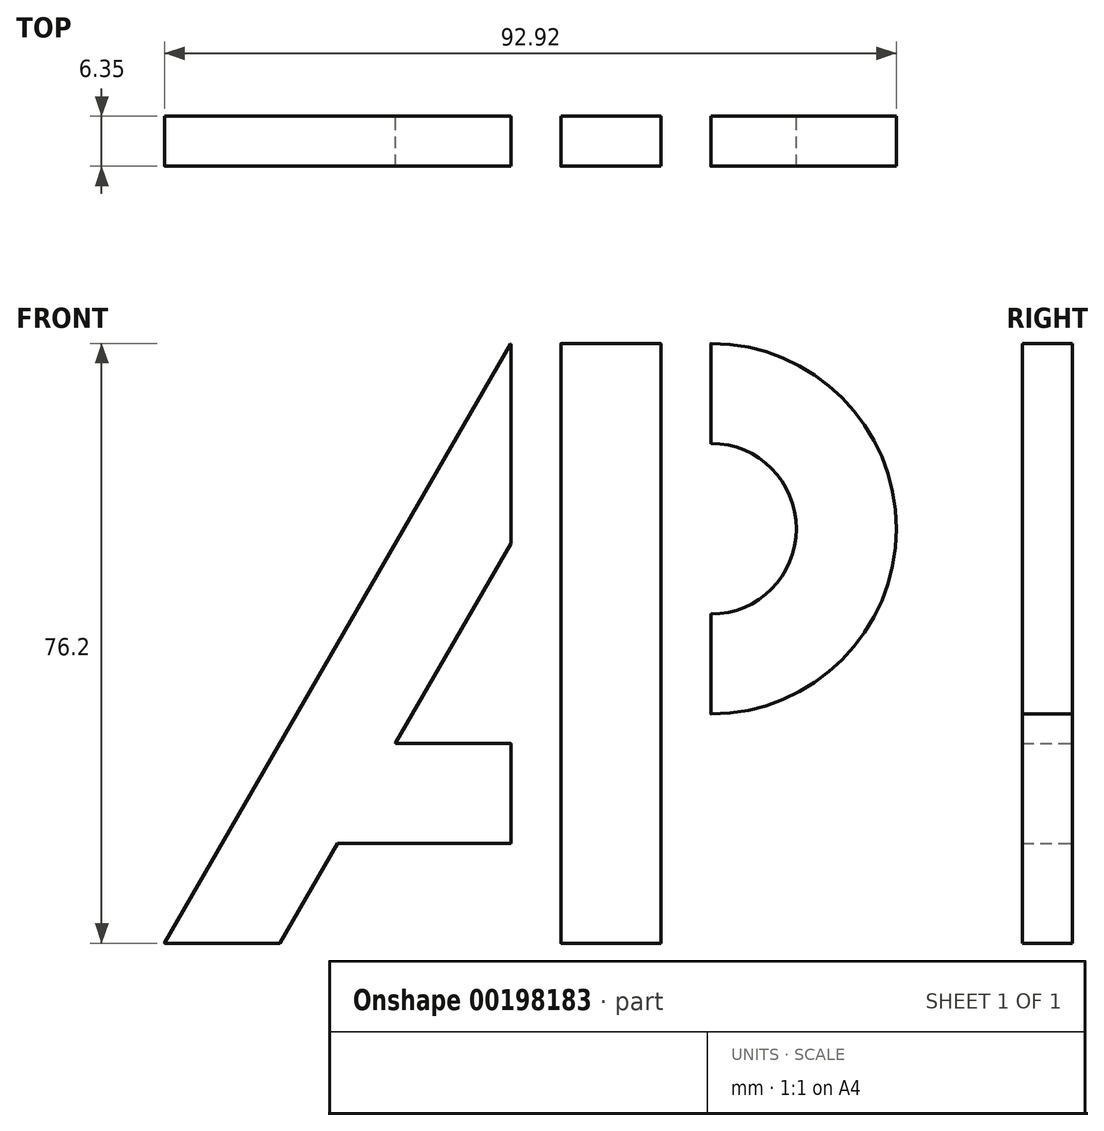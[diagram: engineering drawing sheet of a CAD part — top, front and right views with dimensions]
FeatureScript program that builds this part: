
annotation { "Feature Type Name" : "Feature", "Feature Type Description" : "" }
export const myFeature = defineFeature(function(context is Context, id is Id, definition is map)
    precondition{}
    {
        {
            assignVariable(context, id + "F0", {"name" : "CORNERS", "anyValue" : 1 / 32});
        }
        {
            var Q0;
            Q0=qCreatedBy(makeId("Front.planeOp"),FACE);
            var sketch = newSketch(context, id + "F1", { "sketchPlane" : qUnion([Q0])});
            skLineSegment(sketch, "E0.bottom", {"start": v(-6.35, 38.1) * mm, "end": v(6.35, 38.1) * mm});
            skLineSegment(sketch, "E0.top", {"start": v(-6.35, -38.1) * mm, "end": v(6.35, -38.1) * mm});
            skLineSegment(sketch, "E0.left", {"start": v(-6.35, 38.1) * mm, "end": v(-6.35, -38.1) * mm});
            skLineSegment(sketch, "E0.right", {"start": v(6.35, 38.1) * mm, "end": v(6.35, -38.1) * mm});
            skPoint(sketch, "E0.middle", {"position": v(0, 0) * mm});
            skLineSegment(sketch, "E1.bottom", {"start": v(6.35, 38.1) * mm, "end": v(12.7, 38.1) * mm});
            skLineSegment(sketch, "E1.top", {"start": v(6.35, 25.4) * mm, "end": v(12.7, 25.4) * mm});
            skLineSegment(sketch, "E1.left", {"start": v(6.35, 38.1) * mm, "end": v(6.35, 25.4) * mm});
            skLineSegment(sketch, "E1.right", {"start": v(12.7, 38.1) * mm, "end": v(12.7, 25.4) * mm});
            skLineSegment(sketch, "E2.bottom", {"start": v(6.35, 3.7) * mm, "end": v(12.7, 3.7) * mm});
            skLineSegment(sketch, "E2.top", {"start": v(6.35, -9) * mm, "end": v(12.7, -9) * mm});
            skLineSegment(sketch, "E2.left", {"start": v(6.35, 3.7) * mm, "end": v(6.35, -9) * mm});
            skLineSegment(sketch, "E2.right", {"start": v(12.7, 3.7) * mm, "end": v(12.7, -9) * mm});
            skLineSegment(sketch, "E3.bottom", {"start": v(-6.35, 38.1) * mm, "end": v(-12.7, 38.1) * mm});
            skLineSegment(sketch, "E3.top", {"start": v(-6.35, 12.7) * mm, "end": v(-12.7, 12.7) * mm});
            skLineSegment(sketch, "E3.left", {"start": v(-6.35, 38.1) * mm, "end": v(-6.35, 12.7) * mm});
            skLineSegment(sketch, "E3.right", {"start": v(-12.7, 38.1) * mm, "end": v(-12.7, 12.7) * mm});
            skLineSegment(sketch, "E4.bottom", {"start": v(-6.35, -38.1) * mm, "end": v(-12.7, -38.1) * mm});
            skLineSegment(sketch, "E4.top", {"start": v(-6.35, -25.4) * mm, "end": v(-12.7, -25.4) * mm});
            skLineSegment(sketch, "E4.left", {"start": v(-6.35, -38.1) * mm, "end": v(-6.35, -25.4) * mm});
            skLineSegment(sketch, "E4.right", {"start": v(-12.7, -38.1) * mm, "end": v(-12.7, -25.4) * mm});
            skArc(sketch, "E5", {"start": v(12.7, 3.7) * mm, "mid": v(23.55, 14.55) * mm, "end": v(12.7, 25.4) * mm});
            skArc(sketch, "E6", {"start": v(12.7, -9) * mm, "mid": v(36.25, 14.55) * mm, "end": v(12.7, 38.1) * mm});
            skLineSegment(sketch, "E7", {"start": v(-12.7, -38.1) * mm, "end": v(-56.7, -38.1) * mm});
            skLineSegment(sketch, "E8", {"start": v(-56.7, -38.1) * mm, "end": v(-12.7, 38.1) * mm});
            skLineSegment(sketch, "E9", {"start": v(-12.7, 12.7) * mm, "end": v(-34.7, -25.4) * mm});
            skLineSegment(sketch, "E10", {"start": v(-34.7, -25.4) * mm, "end": v(-12.7, -25.4) * mm});
            skLineSegment(sketch, "E11", {"start": v(-12.7, -25.4) * mm, "end": v(-12.7, -12.7) * mm});
            skLineSegment(sketch, "E12", {"start": v(-12.7, -12.7) * mm, "end": v(-6.35, -12.7) * mm});
            skLineSegment(sketch, "E13", {"start": v(-12.7, -12.7) * mm, "end": v(-27.36, -12.7) * mm});
            skLineSegment(sketch, "E14", {"start": v(-34.7, -25.4) * mm, "end": v(-42.03, -38.1) * mm});
            skSolve(sketch);
        }
        {
            var Q0;
            Q0=makeQuery(id+"F1.imprint","IMPRINT",FACE,{"disambiguationData":[TD([[makeQuery(id+"F1.imprint","IMPRINT",EDGE,{"derivedFrom":sQuery(id+"F1.wireOp",EDGE,"E3.right")}),-1.0]])]});
            var Q1;
            Q1=makeQuery(id+"F1.imprint","IMPRINT",FACE,{"disambiguationData":[TD([[makeQuery(id+"F1.imprint","IMPRINT",EDGE,{"derivedFrom":sQuery(id+"F1.wireOp",EDGE,"E0.bottom")}),-1.0]])]});
            var Q2;
            Q2=makeQuery(id+"F1.imprint","IMPRINT",FACE,{"disambiguationData":[TD([[makeQuery(id+"F1.imprint","IMPRINT",EDGE,{"derivedFrom":sQuery(id+"F1.wireOp",EDGE,"E1.right")}),1.0]])]});
            var Q3;
            {var subQ0=sQuery(id+"F1.wireOp",EDGE,"E10");Q3=makeQuery(id+"F1.imprint","IMPRINT",FACE,{"disambiguationData":[TD([[makeQuery(id+"F1.imprint","IMPRINT",EDGE,{"derivedFrom":subQ0}),1.0]])]});}
            extrude(context, id + "F2", {"entities" : qUnion([Q0, Q1, Q2, Q3]), "depth" : 6.35 * mm});
        }
        {
            var Q0;
            Q0=makeQuery(id+"F2.opExtrude","SWEPT_EDGE",EDGE,{"disambiguationData":[OSD([sQuery(id+"F1.wireOp",EDGE,"E3.bottom"),sQuery(id+"F1.wireOp",EDGE,"E3.right"),sQuery(id+"F1.wireOp",EDGE,"E8")])]});
            var Q1;
            Q1=makeQuery(id+"F2.opExtrude","SWEPT_EDGE",EDGE,{"disambiguationData":[OSD([sQuery(id+"F1.wireOp",EDGE,"E3.top"),sQuery(id+"F1.wireOp",EDGE,"E3.right"),sQuery(id+"F1.wireOp",EDGE,"E9")])]});
            var Q2;
            Q2=makeQuery(id+"F2.opExtrude","SWEPT_EDGE",EDGE,{"disambiguationData":[OSD([sQuery(id+"F1.wireOp",EDGE,"E4.top"),sQuery(id+"F1.wireOp",EDGE,"E4.right"),sQuery(id+"F1.wireOp",EDGE,"E10"),sQuery(id+"F1.wireOp",EDGE,"E11")])]});
            var Q3;
            Q3=makeQuery(id+"F2.opExtrude","SWEPT_EDGE",EDGE,{"disambiguationData":[OSD([sQuery(id+"F1.wireOp",EDGE,"E9"),sQuery(id+"F1.wireOp",EDGE,"E10"),sQuery(id+"F1.wireOp",EDGE,"E14")])]});
            var Q4;
            Q4=makeQuery(id+"F2.opExtrude","SWEPT_EDGE",EDGE,{"disambiguationData":[OSD([sQuery(id+"F1.wireOp",EDGE,"E7"),sQuery(id+"F1.wireOp",EDGE,"E14")])]});
            var Q5;
            Q5=makeQuery(id+"F2.opExtrude","SWEPT_EDGE",EDGE,{"disambiguationData":[OSD([sQuery(id+"F1.wireOp",EDGE,"E7"),sQuery(id+"F1.wireOp",EDGE,"E8")])]});
            var Q6;
            Q6=makeQuery(id+"F2.opExtrude","SWEPT_EDGE",EDGE,{"disambiguationData":[OSD([sQuery(id+"F1.wireOp",EDGE,"E9"),sQuery(id+"F1.wireOp",EDGE,"E13")])]});
            var Q7;
            Q7=makeQuery(id+"F2.opExtrude","SWEPT_EDGE",EDGE,{"disambiguationData":[OSD([sQuery(id+"F1.wireOp",EDGE,"E11"),sQuery(id+"F1.wireOp",EDGE,"E12"),sQuery(id+"F1.wireOp",EDGE,"E13")])]});
            var Q8;
            Q8=makeQuery(id+"F2.opExtrude","SWEPT_EDGE",EDGE,{"disambiguationData":[OSD([sQuery(id+"F1.wireOp",EDGE,"E0.bottom"),sQuery(id+"F1.wireOp",EDGE,"E3.bottom"),sQuery(id+"F1.wireOp",EDGE,"E3.left")])]});
            var Q9;
            Q9=makeQuery(id+"F2.opExtrude","SWEPT_EDGE",EDGE,{"disambiguationData":[OSD([sQuery(id+"F1.wireOp",EDGE,"E0.bottom"),sQuery(id+"F1.wireOp",EDGE,"E1.bottom"),sQuery(id+"F1.wireOp",EDGE,"E1.left")])]});
            var Q10;
            Q10=makeQuery(id+"F2.opExtrude","SWEPT_EDGE",EDGE,{"disambiguationData":[OSD([sQuery(id+"F1.wireOp",EDGE,"E0.top"),sQuery(id+"F1.wireOp",EDGE,"E4.bottom"),sQuery(id+"F1.wireOp",EDGE,"E4.left")])]});
            var Q11;
            Q11=makeQuery(id+"F2.opExtrude","SWEPT_EDGE",EDGE,{"disambiguationData":[OSD([sQuery(id+"F1.wireOp",EDGE,"E0.top"),sQuery(id+"F1.wireOp",EDGE,"E0.right")])]});
            var Q12;
            Q12=makeQuery(id+"F2.opExtrude","SWEPT_EDGE",EDGE,{"disambiguationData":[OSD([sQuery(id+"F1.wireOp",EDGE,"E2.top"),sQuery(id+"F1.wireOp",EDGE,"E2.right"),sQuery(id+"F1.wireOp",EDGE,"E6")])]});
            var Q13;
            Q13=makeQuery(id+"F2.opExtrude","SWEPT_EDGE",EDGE,{"disambiguationData":[OSD([sQuery(id+"F1.wireOp",EDGE,"E2.bottom"),sQuery(id+"F1.wireOp",EDGE,"E2.right"),sQuery(id+"F1.wireOp",EDGE,"E5")])]});
            var Q14;
            Q14=makeQuery(id+"F2.opExtrude","SWEPT_EDGE",EDGE,{"disambiguationData":[OSD([sQuery(id+"F1.wireOp",EDGE,"E1.top"),sQuery(id+"F1.wireOp",EDGE,"E1.right"),sQuery(id+"F1.wireOp",EDGE,"E5")])]});
            var Q15;
            Q15=makeQuery(id+"F2.opExtrude","SWEPT_EDGE",EDGE,{"disambiguationData":[OSD([sQuery(id+"F1.wireOp",EDGE,"E1.bottom"),sQuery(id+"F1.wireOp",EDGE,"E1.right"),sQuery(id+"F1.wireOp",EDGE,"E6")])]});
            fillet(context, id + "F3", {"entities" : qUnion([Q0, Q1, Q2, Q3, Q4, Q5, Q6, Q7, Q8, Q9, Q10, Q11, Q12, Q13, Q14, Q15]), "radius" : (getVariable(context, 'CORNERS')) * mm, "tangentPropagation" : true, "allowEdgeOverflow" : false});
        }
    });
